# Revit family: Faucet-Kitchen_Sink-KOHLER-Simplice-K-647
name_source: partatom
category: Plumbing Fixtures
revit_build: Autodesk Revit 2015 (Build: 20140606_1530(x64)
units: mm (PartAtom-declared; Revit-internal decimal feet)

## types (3) — shared parameters
ADA Compliant = Yes
Assembly Code = D2020
CW Connection = Yes
Cold Water Inlet = Cold Water Inlet
Date Modified = 01/09/2018
Default Elevation = 36"
Description = Two-hole kitchen sink faucet with 16-1/8 inch pull-down swing spout, DockNetik magnetic docking system, and a 3-function sprayhead featuring Sweep spray
Faucet Distance = 8 1/4"
Faucet Handle Distance = 8 1/4"
Faucet Hole Spacing = 8 1/4"
Flow Rate = 2 GPM
HW Connection = Yes
Height = 16 1/8"
Hot Water Inlet = Hot Water Inlet
Length = 10 13/16"
Manufacturer = KOHLER Co.
MasterFormat 1995 = 15410
MasterFormat 2004 = 22.41.39
Material = Premium metal construction
Pressure = 60.00 psi
Product Documentation Link = http://www.us.kohler.com
Product Name = Simplice
Product Page URL = http://www.us.kohler.com
Spout Reach = 9"
URL = https://www.us.kohler.com
Vent Connection = No
Waste Connection = No
Waste Water Outlet = Waste Water Outlet
Width = 2 1/32"

## per-type parameters (varying)
| type | Finish | Model | Type |
| CP-Polished Chrome | Kohler-Metal-CP-Polished_Chrome | K-647-CP | 1 |
| VS-Vibrant Stainless | Kohler-Metal-VS-Vibrant_Stainless | K-647-VS | 2 |
| BL-Matte Black | Kohler-Metal-BL-Matte_Black | K-647-BL | 3 |

## geometry (parser evidence)
native form markers: Sweep x19
no freeform markers — native parametric forms only
